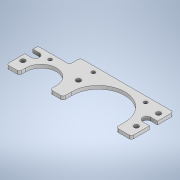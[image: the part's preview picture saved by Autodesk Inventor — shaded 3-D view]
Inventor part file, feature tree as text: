
AUTODESK INVENTOR PART (.ipt)
format: ipt  version: 2021 (Build 250183000, 183)  size: 270,336 bytes
history: native  units: mm
features: sketch x7, extrude x6, hole x2, fillet x2
ambient origin geometry x8: Origin, YZ Plane, XZ Plane, XY Plane, X Axis, Y Axis, Z Axis, Center Point
bodies: Solid1 (feature_tree)
feature tree (17):
  extrude  "Extrusion1"  Depth=112.5mm
  extrude  "Extrusion2"  Depth=47.7mm
  sketch  "Sketch4"  dims[d5=27.7mm d6=27.7mm]
  hole  "Hole1"  [1 undecoded]
  extrude  "Extrusion3"  Depth=27.7mm
  fillet  "Fillet1"  Radius=116.5mm
  hole  "Hole2"  [1 undecoded]
  extrude  "Extrusion4"  Depth=30.9mm
  extrude  "Extrusion5"  Depth=2.0mm
  extrude  "Extrusion6"  Depth=2.0mm
  fillet  "Fillet3"  Radius=35.0mm
  sketch  "Sketch1"  dims[d0=112.5mm d1=116.5mm]
  sketch  "Sketch2"  dims[d2=3.0mm d3=0.0mm d4=47.7mm]
  sketch  "Sketch5"  dims[d7=27.7mm d8=27.7mm d9=116.5mm]
  sketch  "Sketch6"  dims[d10=112.5mm d13=37.0mm]
  sketch  "Sketch7"  dims[d14=18.5mm d15=30.9mm]
  sketch  "Sketch8"  dims[d16=5.0mm d17=0.0mm d18=18.0mm d19=35.0mm d20=35.0mm d43=4.2mm d44=6.0mm d45=4.0mm d46=2.0mm d47=90.0deg d48=8.0mm d49=20.594885mm d50=10.0mm d51=0.0mm d53=28.0mm d54=25.8mm d55=4.7mm d56=5.5mm d57=13.25mm d58=30.0mm d59=50.0mm d60=5.4mm d61=5.4mm d62=18.5mm d63=10.0mm d64=2.0mm d65=27.7mm d66=47.7mm d67=2.0mm d68=27.7mm d69=23.25mm d70=37.0mm d73=20.0mm d74=2.0mm d75=5.5mm d76=5.5mm d77=15.0mm d78=6.5mm d79=36.0mm d80=8.0mm d81=3.2mm d82=6.0mm d83=4.0mm d84=2.0mm d85=90.0deg d86=8.0mm d87=20.594885mm d88=20.0mm d89=28.0mm d90=18.25mm d91=7.2mm d92=7.2mm d93=6.0mm d94=6.0mm d95=10.0mm d96=0.0mm d98=18.5mm d99=45.05mm d100=28.5mm d101=10.0mm d102=10.0mm d103=0.0mm d105=0.3mm d106=0.0mm d107=2.0mm]
note: 2 required parameter values undecoded (feature->parameter linkage not recoverable at this tier; creation-order binding heuristic only, values carry confidence <= 0.55)
